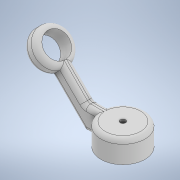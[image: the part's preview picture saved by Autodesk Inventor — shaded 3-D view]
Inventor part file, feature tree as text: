
AUTODESK INVENTOR PART (.ipt)
format: ipt  version: 2022 (Build 260153000, 153)  size: 227,840 bytes
history: native  units: mm
features: extrude x7, sketch x7, fillet x2, other x1
ambient origin geometry x8: Origin, YZ Plane, XZ Plane, XY Plane, X Axis, Y Axis, Z Axis, Center Point
bodies: Body1 (feature_tree)
feature tree (17):
  other  "Bryła1"
  extrude  "Wyciągnięcie proste1"  Depth=40.0mm
  extrude  "Wyciągnięcie proste2"  Depth=20.0mm TaperAngle=0.0deg
  extrude  "Wyciągnięcie proste3"  Depth=30.0mm
  extrude  "Wyciągnięcie proste4"  Depth=20.0mm
  extrude  "Wyciągnięcie proste6"  TaperAngle=45.0deg  [1 undecoded]
  fillet  "Zaokrąglenie1"  Radius=10.0mm
  extrude  "Wyciągnięcie proste7"  Depth=90.0mm
  fillet  "Zaokrąglenie2"  Radius=22.0mm
  extrude  "Wyciągnięcie proste8"  Depth=5.0mm
  sketch  "Szkic1"
  sketch  "Szkic2"
  sketch  "Szkic3"
  sketch  "Szkic4"
  sketch  "Szkic6"
  sketch  "Szkic7"
  sketch  "Szkic8"
note: 1 required parameter value undecoded (feature->parameter linkage not recoverable at this tier; creation-order binding heuristic only, values carry confidence <= 0.55)
